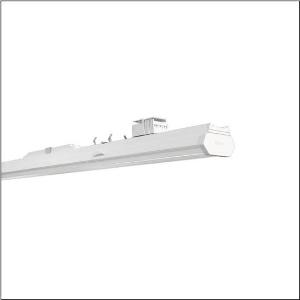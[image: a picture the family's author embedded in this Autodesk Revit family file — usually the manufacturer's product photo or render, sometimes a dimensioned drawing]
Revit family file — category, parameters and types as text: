
# Revit family: licross_11_protected_mo_51td12dn495g3s4
name_source: partatom
category: Lighting Fixtures
units: mm (PartAtom-declared; Revit-internal decimal feet)

## family parameters
Cut with Voids When Loaded = No
Host = Face
Light Source = No
Part Type = Normal
Room Calculation Point = No
Round Connector Dimension = Use Diameter
Shared = No

## types (1)
- --- (1 x LED, 980 lm, 6.8 W, 4000K)
    Apparent Load = 7 VA
    CIE Flux Codes = 73 92 98 99 100
    Color Rendering = 80
    Color Temperature = 4000K
    Default Elevation = 1800 mm
    Description = Licross 11 Protected MO, luminaire insert, of sheet steel, galvanised, coil coated, white, length: 1.500mm, width: 90mm, height: 101mm, LED rated luminous flux: 9.980lm, light colour: 840, SDCM (Standard Deviation of Colour Matching)MacAdam ≤ 2 SDCM (initial), control gear: DALI 2, with plug, 6-pole, with phase selection, for trunking rail, 9 or 11-core, mains connection: 220..240V, AC, 50/60Hz, rated input power: 61W, for trunking rail, 9-/11-core, internal wiring halogen-free, for emergency light function, converter,control gear: single battery element, battery: LiFePO4, 9Ah, primary light control with lens, of plastic, primary optical cover: cover, of PMMA, light emission: direct distribution, primary light characteristic: symmetric, protection rating (complete): IP54, insulation class (complete): insulation class I (protective earthing), certification: CE, UKCA, protection symbol: D if used in an environment with non-conductive dust loads with corresponding accessories, impact resistance: IK06, permissible ambient temperature for indoor applications: +5..+35°C, standard: EN 60598-2-22, LABS conformity tested according to VDMA 24364:2018-05, reducing of maximum allowable ambient temperature of 5°C with ceiling mounting, corresponds to IFS (International Featured Standards) requirements for safety and quality in the food industry, The light source and the operating device comply with the requirements of the Ecodesign Regulation (EU) 2019/2020 and are replaceable in accordance with this regulation, packaging unit: 1 piece
    Height = 92 mm
    Lamp = 1 x LED
    Lamp Light Flux = 980 lm
    Lamp Power = 6.8 W
    Lamp count = 1
    Length = 1500 mm
    Luminous efficacy = 144 lm/W
    Manufacturer = Siteco
    ModVariant = No
    Model = 51TD12DN495G3S4
    Mounting Place = Ceiling
    Mounting Type = Pendant
    Number of Poles = 1
    OnlyDefault = Yes
    Power Factor = 1
    Product Name = Licross 11 Protected MO
    Product group = luminaire insert | ceiling pendant
    ProductGroupID = 901
    Protection Class = Protection class I
    Protection Degree = IP 54
    RLX_Detail_Level = 1
    RLX_Emergency_Light_Flux = 0 lm
    RLX_Emergency_Type = 0
    RLX_Emergency_Type_DB = No
    RlxData = <blob elided: 25169 chars, md5=4ebc88cb>
    Socket = socket
    Standby Power = 0 W
    System Light Flux = 980 lm
    System Power = 7 W
    Type Comments = : emergency light operation: 3 h
    Type Image = l_1256145.jpg
    URL = http://relux.com
    VarID = @adj_095993
    Voltage = 0 V
    Weight = 0.00 kg
    Width = 88 mm

## geometry (parser evidence)
native form markers: Blend x4, Sweep x9
no freeform markers — native parametric forms only
